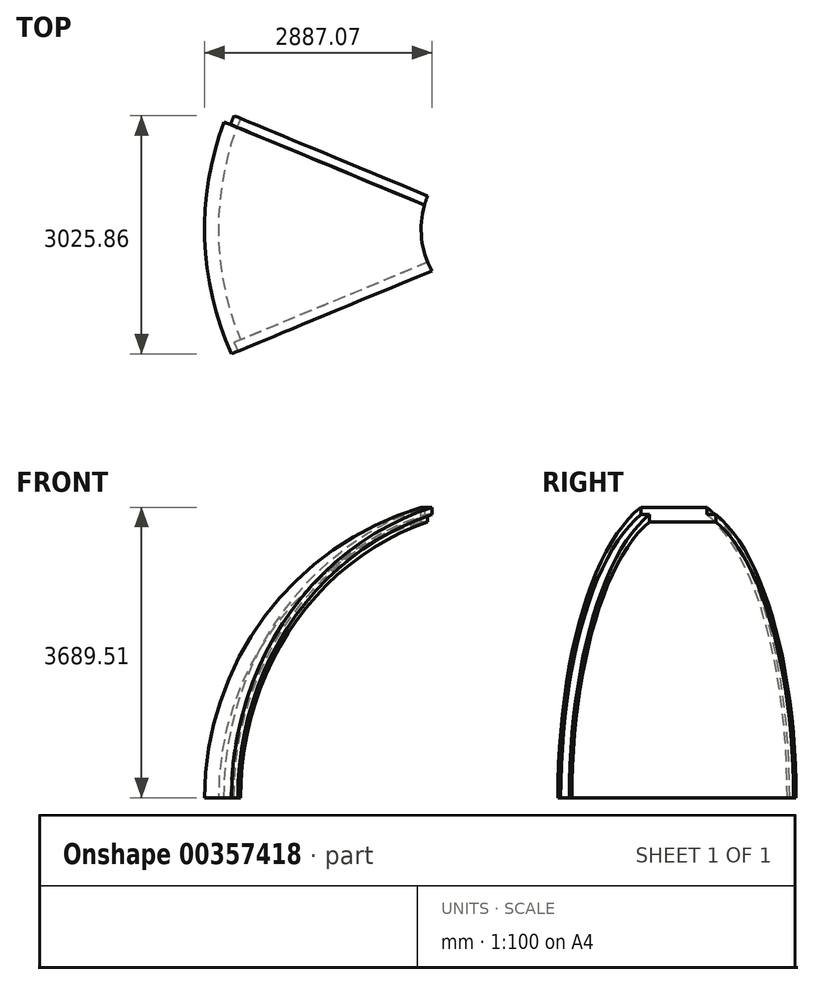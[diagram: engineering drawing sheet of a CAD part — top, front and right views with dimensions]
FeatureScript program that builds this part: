
annotation { "Feature Type Name" : "Feature", "Feature Type Description" : "" }
export const myFeature = defineFeature(function(context is Context, id is Id, definition is map)
    precondition{}
    {
        {
            var Q0;
            Q0=qCreatedBy(makeId("Top.planeOp"),FACE);
            var sketch = newSketch(context, id + "F0", { "sketchPlane" : qUnion([Q0])});
            skCircle(sketch, "E0", {"center": v(0, 0) * mm, "radius": 3850 * mm});
            skCircle(sketch, "E1", {"center": v(0, 0) * mm, "radius": 1000 * mm});
            skLineSegment(sketch, "E2", {"start": v(0, 3850) * mm, "end": v(0, -3850) * mm});
            skLineSegment(sketch, "E3", {"start": v(-3850, 0) * mm, "end": v(3850, 0) * mm});
            skLineSegment(sketch, "E4", {"start": v(2722.36, 2722.36) * mm, "end": v(-2722.36, -2722.36) * mm});
            skLineSegment(sketch, "E5", {"start": v(-2722.36, 2722.36) * mm, "end": v(2722.36, -2722.36) * mm});
            skSolve(sketch);
        }
        {
            var Q0;
            Q0=qCreatedBy(makeId("Front.planeOp"),FACE);
            var sketch = newSketch(context, id + "F1", { "sketchPlane" : qUnion([Q0])});
            skArc(sketch, "E6", {"start": v(3850, 0) * mm, "mid": v(0, 3850) * mm, "end": v(-3850, 0) * mm});
            skSolve(sketch);
        }
        {
            var Q0;
            Q0=qCreatedBy(makeId("Front.planeOp"),FACE);
            var sketch = newSketch(context, id + "F2", { "sketchPlane" : qUnion([Q0])});
            skArc(sketch, "E7.0", {"start": v(-1000, 3717.86) * mm, "mid": v(-3055.53, 2342.27) * mm, "end": v(-3850, 0) * mm});
            skLineSegment(sketch, "E8", {"start": v(-3675, 0) * mm, "end": v(-3850, 0) * mm});
            skArc(sketch, "E9.0", {"start": v(-1000, 3536.33) * mm, "mid": v(-2930.92, 2217.05) * mm, "end": v(-3675, 0) * mm});
            skLineSegment(sketch, "E10", {"start": v(0, 3675) * mm, "end": v(0, 3850) * mm, "construction": true});
            skPoint(sketch, "E11.orphan", {"position": v(3850, 0) * mm});
            skLineSegment(sketch, "E12", {"start": v(-1000, 3717.86) * mm, "end": v(-1000, 3536.33) * mm});
            skSolve(sketch);
        }
        {
            var Q0;
            Q0 = qSketchRegion(id + "F2", true);
            var Q1;
            Q1=sQuery(id+"F2.wireOp",EDGE,"E10");
            revolve(context, id + "F3", {"entities" : qUnion([Q0]), "axis" : qUnion([Q1]), "revolveType" : RevolveType.SYMMETRIC, "angle" : 45 * degree});
        }
        {
            var Q0;
            Q0=makeQuery(id+"F3.opRevolve","SWEPT_FACE",FACE,{"disambiguationData":[OSD([sQuery(id+"F2.wireOp",EDGE,"E8")])]});
            var sketch = newSketch(context, id + "F4", { "sketchPlane" : qUnion([Q0])});
            skArc(sketch, "E13", {"start": v(-3520.24, -1328.26) * mm, "mid": v(-3498.62, -1384.23) * mm, "end": v(-3476.1, -1439.85) * mm});
            skArc(sketch, "E14.0", {"start": v(-3602.11, -1359.15) * mm, "mid": v(-3579.98, -1416.42) * mm, "end": v(-3556.94, -1473.33) * mm});
            skLineSegment(sketch, "E15", {"start": v(-3476.1, -1439.85) * mm, "end": v(-3556.94, -1473.33) * mm});
            skLineSegment(sketch, "E16", {"start": v(-3520.24, -1328.26) * mm, "end": v(-3602.11, -1359.15) * mm});
            skPoint(sketch, "E17.orphan", {"position": v(-3556.94, 1473.33) * mm});
            skSolve(sketch);
        }
        {
            var Q0;
            Q0=makeQuery(id+"F4.imprint","IMPRINT",FACE,{"disambiguationData":[TD([[makeQuery(id+"F4.imprint","IMPRINT",EDGE,{"derivedFrom":sQuery(id+"F4.wireOp",EDGE,"E13")}),-1.0]])]});
            var Q1;
            Q1=makeQuery(id+"F3.opRevolve","CAP_EDGE",EDGE,{"disambiguationData":[OSD([sQuery(id+"F2.wireOp",EDGE,"E7.0")])],"isStart":true});
            sweep(context, id + "F5", {"operationType" : NewBodyOperationType.REMOVE, "profiles" : qUnion([Q0]), "path" : qUnion([Q1])});
        }
        {
            var Q0;
            Q0=makeQuery(id+"F3.opRevolve","SWEPT_FACE",FACE,{"disambiguationData":[OSD([sQuery(id+"F2.wireOp",EDGE,"E8")])]});
            var sketch = newSketch(context, id + "F6", { "sketchPlane" : qUnion([Q0])});
            skArc(sketch, "E18.0", {"start": v(-3508.14, 1586.01) * mm, "mid": v(-3532.99, 1529.87) * mm, "end": v(-3556.94, 1473.33) * mm});
            skArc(sketch, "E19", {"start": v(-3428.41, 1549.97) * mm, "mid": v(-3452.7, 1495.1) * mm, "end": v(-3476.1, 1439.85) * mm});
            skLineSegment(sketch, "E20", {"start": v(-3428.41, 1549.97) * mm, "end": v(-3508.14, 1586.01) * mm});
            skPoint(sketch, "E21.orphan", {"position": v(-3556.94, 1473.33) * mm});
            skLineSegment(sketch, "E22.0", {"start": v(-3476.1, 1439.85) * mm, "end": v(-3556.94, 1473.33) * mm});
            skPoint(sketch, "E23.orphan", {"position": v(-3602.11, -1359.15) * mm});
            skPoint(sketch, "E24.orphan", {"position": v(-3395.26, 1406.36) * mm});
            skSolve(sketch);
        }
        {
            var Q0;
            Q0=makeQuery(id+"F6.imprint","IMPRINT",FACE,{"disambiguationData":[TD([[makeQuery(id+"F6.imprint","IMPRINT",EDGE,{"derivedFrom":sQuery(id+"F6.wireOp",EDGE,"E18.0")}),1.0]])]});
            var Q1;
            Q1=makeQuery(id+"F3.opRevolve","CAP_EDGE",EDGE,{"disambiguationData":[OSD([sQuery(id+"F2.wireOp",EDGE,"E7.0")])],"isStart":false});
            sweep(context, id + "F7", {"operationType" : NewBodyOperationType.ADD, "profiles" : qUnion([Q0]), "path" : qUnion([Q1])});
        }
        {
            var Q0;
            Q0=qCreatedBy(makeId("Front.planeOp"),FACE);
            var sketch = newSketch(context, id + "F8", { "sketchPlane" : qUnion([Q0])});
            skLineSegment(sketch, "E25", {"start": v(0, 0) * mm, "end": v(0, 4000) * mm});
            skLineSegment(sketch, "E26", {"start": v(0, 4000) * mm, "end": v(-1100, 4000) * mm});
            skLineSegment(sketch, "E27", {"start": v(-1100, 4000) * mm, "end": v(-1100, 0) * mm});
            skLineSegment(sketch, "E28", {"start": v(-1100, 0) * mm, "end": v(0, 0) * mm});
            skSolve(sketch);
        }
        {
            var Q0;
            Q0 = qSketchRegion(id + "F8", true);
            var Q1;
            Q1=sQuery(id+"F8.wireOp",EDGE,"E25");
            revolve(context, id + "F9", {"operationType" : NewBodyOperationType.REMOVE, "entities" : qUnion([Q0]), "axis" : qUnion([Q1]), "revolveType" : RevolveType.FULL, "oppositeDirection" : true});
        }
    });
